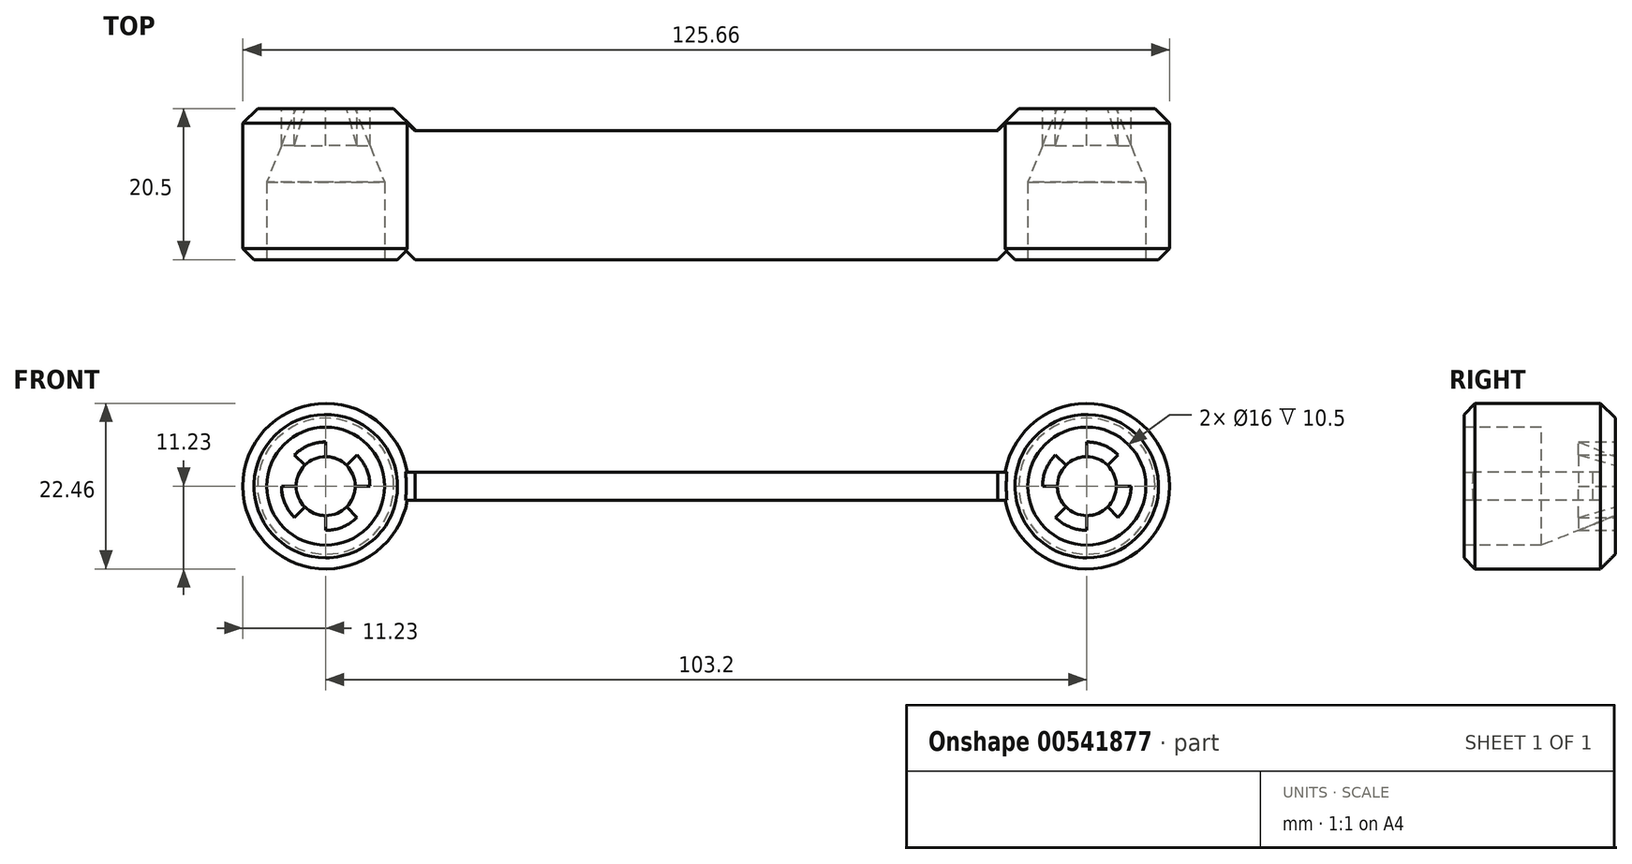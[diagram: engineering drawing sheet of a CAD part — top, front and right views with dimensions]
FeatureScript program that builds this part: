
annotation { "Feature Type Name" : "Feature", "Feature Type Description" : "" }
export const myFeature = defineFeature(function(context is Context, id is Id, definition is map)
    precondition{}
    {
        {
            var Q0;
            Q0=qCreatedBy(makeId("Top.planeOp"),FACE);
            var sketch = newSketch(context, id + "F0", { "sketchPlane" : qUnion([Q0])});
            skLineSegment(sketch, "E0", {"start": v(90.5, 20.5) * mm, "end": v(97.73, 20.5) * mm});
            skLineSegment(sketch, "E1", {"start": v(90.5, 20.5) * mm, "end": v(94.5, 10.5) * mm});
            skLineSegment(sketch, "E2", {"start": v(86.5, 10.5) * mm, "end": v(86.5, 25.55) * mm});
            skLineSegment(sketch, "E3.0", {"start": v(0, 10.5) * mm, "end": v(0, 25.55) * mm});
            skLineSegment(sketch, "E4", {"start": v(97.73, 20.5) * mm, "end": v(97.73, 0) * mm});
            skLineSegment(sketch, "E5", {"start": v(94.5, 10.5) * mm, "end": v(94.5, 0) * mm});
            skLineSegment(sketch, "E6", {"start": v(94.5, 0) * mm, "end": v(97.73, 0) * mm});
            skPoint(sketch, "E7.0.end.orphan", {"position": v(97.73, 10.5) * mm});
            skPoint(sketch, "E7.0.start.orphan", {"position": v(93.73, 20.5) * mm});
            skSolve(sketch);
        }
        {
            var Q0;
            Q0=makeQuery(id+"F0.imprint","IMPRINT",FACE,{"disambiguationData":[TD([[makeQuery(id+"F0.imprint","IMPRINT",EDGE,{"derivedFrom":sQuery(id+"F0.wireOp",EDGE,"E0")}),-1.0]])]});
            var Q1;
            Q1=sQuery(id+"F0.wireOp",EDGE,"E2");
            revolve(context, id + "F1", {"entities" : qUnion([Q0]), "axis" : qUnion([Q1]), "revolveType" : RevolveType.FULL});
        }
        {
            var Q0;
            Q0=makeQuery(id+"FqM3FLzhflj6yz1_1.opRevolve","SWEPT_EDGE",EDGE,{"disambiguationData":[OSD([sQuery(id+"F0.wireOp",EDGE,"b2d47922-1eca-4d70-a656-72b89438e9751.MirrorCS"),sQuery(id+"F0.wireOp",EDGE,"b2d47922-1eca-4d70-a656-72b89438e9752.MirrorCS")])]});
            var Q1;
            Q1=makeQuery(id+"F1.opRevolve","SWEPT_EDGE",EDGE,{"disambiguationData":[OSD([sQuery(id+"F0.wireOp",EDGE,"E4"),sQuery(id+"F0.wireOp",EDGE,"E6")])]});
            chamfer(context, id + "F2", {"entities" : qUnion([Q0, Q1]), "width" : 1.5 * mm, "tangentPropagation" : true});
        }
        {
            var Q0;
            Q0=qCreatedBy(makeId("Front.planeOp"),FACE);
            var sketch = newSketch(context, id + "F3", { "sketchPlane" : qUnion([Q0])});
            skLineSegment(sketch, "E8", {"start": v(42, 1.92) * mm, "end": v(-42, 1.92) * mm});
            skLineSegment(sketch, "E9.MirrorCS", {"start": v(42, -1.92) * mm, "end": v(-42, -1.92) * mm});
            skLineSegment(sketch, "E10", {"start": v(-42, 1.92) * mm, "end": v(-42, -1.92) * mm});
            skLineSegment(sketch, "E11", {"start": v(42, 1.92) * mm, "end": v(42, -1.92) * mm});
            skSolve(sketch);
        }
        {
            var Q0;
            Q0=makeQuery(id+"FqM3FLzhflj6yz1_1.opRevolve","SWEPT_EDGE",EDGE,{"disambiguationData":[OSD([sQuery(id+"F0.wireOp",EDGE,"2ee44e68-2fa0-44c4-b45e-b1434726b3df1.MirrorCS"),sQuery(id+"F0.wireOp",EDGE,"b2d47922-1eca-4d70-a656-72b89438e9751.MirrorCS")])]});
            var Q1;
            Q1=makeQuery(id+"F1.opRevolve","SWEPT_EDGE",EDGE,{"disambiguationData":[OSD([sQuery(id+"F0.wireOp",EDGE,"E0"),sQuery(id+"F0.wireOp",EDGE,"E4")])]});
            chamfer(context, id + "F4", {"entities" : qUnion([Q0, Q1]), "width" : 2 * mm, "tangentPropagation" : true});
        }
        {
            var Q0;
            Q0=makeQuery(id+"F3.imprint","IMPRINT",FACE,{"disambiguationData":[TD([[makeQuery(id+"F3.imprint","IMPRINT",EDGE,{"derivedFrom":sQuery(id+"F3.wireOp",EDGE,"E8")}),1.0]])]});
            extrude(context, id + "F5", {"entities" : qUnion([Q0]), "oppositeDirection" : true, "depth" : 17.5 * mm, "offsetDistance" : 25 * mm});
        }
        {
            var Q0;
            Q0=makeQuery(id+"F1.opRevolve","SWEPT_FACE",FACE,{"disambiguationData":[OSD([sQuery(id+"F0.wireOp",EDGE,"E0")])]});
            var sketch = newSketch(context, id + "F6", { "sketchPlane" : qUnion([Q0])});
            skLineSegment(sketch, "E12", {"start": v(-86.5, 0) * mm, "end": v(-86.5, 11.97) * mm});
            skCircle(sketch, "E13", {"center": v(-86.5, 0) * mm, "radius": 6 * mm});
            skLineSegment(sketch, "E14.1.0", {"start": v(-86.5, 0) * mm, "end": v(-94.96, 8.46) * mm});
            skLineSegment(sketch, "E14.2.0", {"start": v(-86.5, 0) * mm, "end": v(-98.47, 0) * mm});
            skLineSegment(sketch, "E14.3.0", {"start": v(-86.5, 0) * mm, "end": v(-94.96, -8.46) * mm});
            skLineSegment(sketch, "E14.4.0", {"start": v(-86.5, 0) * mm, "end": v(-86.5, -11.97) * mm});
            skLineSegment(sketch, "E14.5.0", {"start": v(-86.5, 0) * mm, "end": v(-78.04, -8.46) * mm});
            skLineSegment(sketch, "E14.6.0", {"start": v(-86.5, 0) * mm, "end": v(-74.53, 0) * mm});
            skLineSegment(sketch, "E14.7.0", {"start": v(-86.5, 0) * mm, "end": v(-78.04, 8.46) * mm});
            skSolve(sketch);
        }
        {
            var Q0;
            {var subQ0=sQuery(id+"F6.wireOp",EDGE,"E13");var subQ1=sQuery(id+"F6.wireOp",EDGE,"E12");var subQ2=makeQuery(id+"F6.imprint","INTERSECT",VERTEX,{"derivedFrom":[subQ1,subQ0]});Q0=makeQuery(id+"F6.imprint","IMPRINT",FACE,{"disambiguationData":[TD([[makeQuery(id+"F6.imprint","IMPRINT",EDGE,{"disambiguationData":[TD([[subQ2,-1.0]])],"derivedFrom":subQ0}),1.0]])]});}
            var Q1;
            {var subQ0=sQuery(id+"F6.wireOp",EDGE,"E14.2.0");var subQ1=sQuery(id+"F6.wireOp",EDGE,"E13");var subQ2=makeQuery(id+"F6.imprint","INTERSECT",VERTEX,{"derivedFrom":[subQ1,subQ0]});Q1=makeQuery(id+"F6.imprint","IMPRINT",FACE,{"disambiguationData":[TD([[makeQuery(id+"F6.imprint","IMPRINT",EDGE,{"disambiguationData":[TD([[subQ2,-1.0]])],"derivedFrom":subQ1}),1.0]])]});}
            var Q2;
            {var subQ0=sQuery(id+"F6.wireOp",EDGE,"E14.4.0");var subQ1=sQuery(id+"F6.wireOp",EDGE,"E13");var subQ2=makeQuery(id+"F6.imprint","INTERSECT",VERTEX,{"derivedFrom":[subQ1,subQ0]});Q2=makeQuery(id+"F6.imprint","IMPRINT",FACE,{"disambiguationData":[TD([[makeQuery(id+"F6.imprint","IMPRINT",EDGE,{"disambiguationData":[TD([[subQ2,-1.0]])],"derivedFrom":subQ1}),1.0]])]});}
            var Q3;
            {var subQ0=sQuery(id+"F6.wireOp",EDGE,"E14.7.0");var subQ1=sQuery(id+"F6.wireOp",EDGE,"E13");var subQ2=makeQuery(id+"F6.imprint","INTERSECT",VERTEX,{"derivedFrom":[subQ1,subQ0]});Q3=makeQuery(id+"F6.imprint","IMPRINT",FACE,{"disambiguationData":[TD([[makeQuery(id+"F6.imprint","IMPRINT",EDGE,{"disambiguationData":[TD([[subQ2,1.0]])],"derivedFrom":subQ1}),1.0]])]});}
            extrude(context, id + "F7", {"entities" : qUnion([Q0, Q1, Q2, Q3]), "operationType" : NewBodyOperationType.REMOVE, "oppositeDirection" : true, "depth" : 10 * mm, "offsetDistance" : 25 * mm});
        }
        {
            var Q0;
            Q0=makeQuery(id+"F5.opExtrude","CAP_EDGE",EDGE,{"disambiguationData":[OSD([sQuery(id+"F3.wireOp",EDGE,"E11")])],"isStart":true});
            var Q1;
            Q1=makeQuery(id+"F5.opExtrude","CAP_EDGE",EDGE,{"disambiguationData":[OSD([sQuery(id+"F3.wireOp",EDGE,"E10")])],"isStart":true});
            chamfer(context, id + "F8", {"entities" : qUnion([Q0, Q1]), "width" : 2.5 * mm, "tangentPropagation" : true});
        }
        {
            var Q0;
            Q0=makeQuery(id+"F1.opRevolve","SWEPT_BODY",BODY,{"disambiguationData":[OSD([sQuery(id+"F0.wireOp",EDGE,"E0"),sQuery(id+"F0.wireOp",EDGE,"E1"),sQuery(id+"F0.wireOp",EDGE,"E4"),sQuery(id+"F0.wireOp",EDGE,"E5"),sQuery(id+"F0.wireOp",EDGE,"E6")])]});
            transform(context, id + "F9", {"entities" : qUnion([Q0]), "transformType" : TransformType.TRANSLATION_3D, "dx" : -34.9 * mm, "dy" : 0 * mm, "dz" : 0 * mm, "makeCopy" : false});
        }
        {
            var Q0;
            Q0=makeQuery(id+"F1.opRevolve","SWEPT_BODY",BODY,{"disambiguationData":[OSD([sQuery(id+"F0.wireOp",EDGE,"E0"),sQuery(id+"F0.wireOp",EDGE,"E1"),sQuery(id+"F0.wireOp",EDGE,"E4"),sQuery(id+"F0.wireOp",EDGE,"E5"),sQuery(id+"F0.wireOp",EDGE,"E6")])]});
            var Q1;
            Q1=qCreatedBy(makeId("Right.planeOp"),FACE);
            mirror(context, id + "F10", {"operationType" : NewBodyOperationType.ADD, "entities" : qUnion([Q0]), "mirrorPlane" : qUnion([Q1])});
        }
        {
            var Q0;
            Q0=makeQuery(id+"F10.boolean.opBoolean","INTERSECT",EDGE,{"derivedFrom":[makeQuery(id+"F1.opRevolve","SWEPT_FACE",FACE,{"disambiguationData":[OSD([sQuery(id+"F0.wireOp",EDGE,"E4")])]}),makeQuery(id+"F5.opExtrude","CAP_FACE",FACE,{"disambiguationData":[OSD([sQuery(id+"F3.wireOp",EDGE,"E8"),sQuery(id+"F3.wireOp",EDGE,"E9.MirrorCS"),sQuery(id+"F3.wireOp",EDGE,"E10"),sQuery(id+"F3.wireOp",EDGE,"E11")])],"isStart":false})]});
            var Q1;
            Q1=makeQuery(id+"F10.boolean.opBoolean","INTERSECT",EDGE,{"derivedFrom":[makeQuery(id+"F5.opExtrude","CAP_FACE",FACE,{"disambiguationData":[OSD([sQuery(id+"F3.wireOp",EDGE,"E8"),sQuery(id+"F3.wireOp",EDGE,"E9.MirrorCS"),sQuery(id+"F3.wireOp",EDGE,"E10"),sQuery(id+"F3.wireOp",EDGE,"E11")])],"isStart":false}),makeQuery(id+"F10.opPattern","COPY",FACE,{"derivedFrom":makeQuery(id+"F1.opRevolve","SWEPT_FACE",FACE,{"disambiguationData":[OSD([sQuery(id+"F0.wireOp",EDGE,"E4")])]}),"instanceName":"1"})]});
            chamfer(context, id + "F11", {"entities" : qUnion([Q0, Q1]), "width" : 1 * mm, "tangentPropagation" : true});
        }
    });
